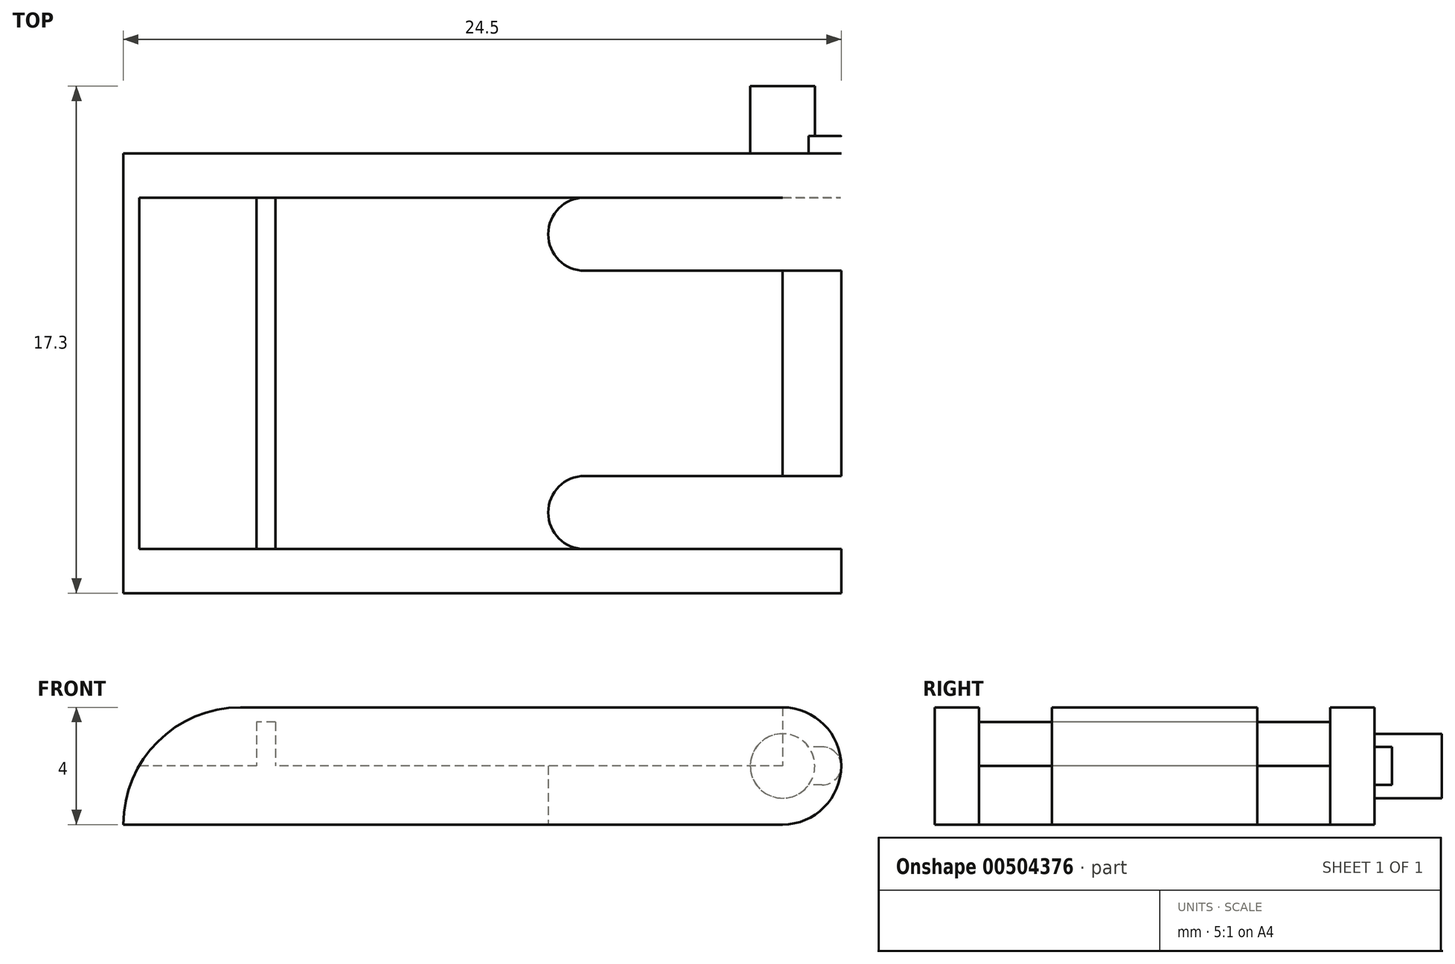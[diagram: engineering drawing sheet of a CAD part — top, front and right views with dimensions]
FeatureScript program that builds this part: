
annotation { "Feature Type Name" : "Feature", "Feature Type Description" : "" }
export const myFeature = defineFeature(function(context is Context, id is Id, definition is map)
    precondition{}
    {
        {
            var Q0;
            Q0=qCreatedBy(makeId("Top.planeOp"),FACE);
            var sketch = newSketch(context, id + "F0", { "sketchPlane" : qUnion([Q0])});
            skLineSegment(sketch, "E0.bottom", {"start": v(0, 0) * mm, "end": v(24.5, 0) * mm});
            skLineSegment(sketch, "E0.top", {"start": v(0, -15) * mm, "end": v(24.5, -15) * mm});
            skLineSegment(sketch, "E0.left", {"start": v(0, 0) * mm, "end": v(0, -15) * mm});
            skLineSegment(sketch, "E0.right", {"start": v(24.5, 0) * mm, "end": v(24.5, -15) * mm});
            skSolve(sketch);
        }
        {
            var Q0;
            Q0=makeQuery(id+"F0.imprint","IMPRINT",FACE,{"disambiguationData":[TD([[makeQuery(id+"F0.imprint","IMPRINT",EDGE,{"derivedFrom":sQuery(id+"F0.wireOp",EDGE,"E0.bottom")}),-1.0]])]});
            extrude(context, id + "F1", {"entities" : qUnion([Q0]), "depth" : 4 * mm});
        }
        {
            var Q0;
            Q0=makeQuery(id+"F1.opExtrude","CAP_FACE",FACE,{"disambiguationData":[OSD([sQuery(id+"F0.wireOp",EDGE,"E0.bottom"),sQuery(id+"F0.wireOp",EDGE,"E0.top"),sQuery(id+"F0.wireOp",EDGE,"E0.left"),sQuery(id+"F0.wireOp",EDGE,"E0.right")])],"isStart":true});
            var sketch = newSketch(context, id + "F2", { "sketchPlane" : qUnion([Q0])});
            skLineSegment(sketch, "E1.bottom", {"start": v(24.5, 11) * mm, "end": v(15.75, 11) * mm});
            skLineSegment(sketch, "E1.top", {"start": v(24.5, 4) * mm, "end": v(15.75, 4) * mm});
            skArc(sketch, "E2", {"start": v(15.75, 13.5) * mm, "mid": v(14.5, 12.25) * mm, "end": v(15.75, 11) * mm});
            skArc(sketch, "E3", {"start": v(15.75, 4) * mm, "mid": v(14.5, 2.75) * mm, "end": v(15.75, 1.5) * mm});
            skLineSegment(sketch, "E4", {"start": v(15.75, 1.5) * mm, "end": v(24.5, 1.5) * mm});
            skLineSegment(sketch, "E5", {"start": v(15.75, 13.5) * mm, "end": v(24.5, 13.5) * mm});
            skLineSegment(sketch, "E6", {"start": v(24.5, 13.5) * mm, "end": v(24.5, 11) * mm});
            skLineSegment(sketch, "E7.trimOffspring", {"start": v(24.5, 4) * mm, "end": v(24.5, 1.5) * mm});
            skLineSegment(sketch, "E8", {"start": v(24.5, 1.5) * mm, "end": v(24.5, 0) * mm, "construction": true});
            skLineSegment(sketch, "E9", {"start": v(24.5, 13.5) * mm, "end": v(24.5, 15) * mm, "construction": true});
            skSolve(sketch);
        }
        {
            var Q0;
            Q0=makeQuery(id+"F2.imprint","IMPRINT",FACE,{"disambiguationData":[TD([[makeQuery(id+"F2.imprint","IMPRINT",EDGE,{"derivedFrom":sQuery(id+"F2.wireOp",EDGE,"E1.bottom")}),-1.0]])]});
            var Q1;
            Q1=makeQuery(id+"F2.imprint","IMPRINT",FACE,{"disambiguationData":[TD([[makeQuery(id+"F2.imprint","IMPRINT",EDGE,{"derivedFrom":sQuery(id+"F2.wireOp",EDGE,"E1.top")}),1.0]])]});
            extrude(context, id + "F3", {"entities" : qUnion([Q0, Q1]), "operationType" : NewBodyOperationType.REMOVE, "oppositeDirection" : true, "depth" : 25 * mm});
        }
        {
            var Q0;
            {var subQ0=sQuery(id+"F0.wireOp",EDGE,"E0.right");var subQ1=sQuery(id+"F0.wireOp",EDGE,"E0.top");Q0=makeQuery(id+"F3.boolean.opBoolean","SPLIT",EDGE,{"disambiguationData":[TD([makeQuery(id+"F1.opExtrude","SWEPT_FACE",FACE,{"disambiguationData":[OSD([subQ1])]})])],"derivedFrom":makeQuery(id+"F1.opExtrude","CAP_EDGE",EDGE,{"disambiguationData":[OSD([subQ0])],"isStart":true})});}
            var Q1;
            {var subQ0=sQuery(id+"F0.wireOp",EDGE,"E0.right");var subQ1=sQuery(id+"F0.wireOp",EDGE,"E0.top");Q1=makeQuery(id+"F3.boolean.opBoolean","SPLIT",EDGE,{"disambiguationData":[TD([makeQuery(id+"F1.opExtrude","SWEPT_FACE",FACE,{"disambiguationData":[OSD([subQ1])]})])],"derivedFrom":makeQuery(id+"F1.opExtrude","CAP_EDGE",EDGE,{"disambiguationData":[OSD([subQ0])],"isStart":false})});}
            var Q2;
            {var subQ0=sQuery(id+"F0.wireOp",EDGE,"E0.right");Q2=makeQuery(id+"F3.boolean.opBoolean","SPLIT",EDGE,{"disambiguationData":[TD([makeQuery(id+"F3.opExtrude","SWEPT_FACE",FACE,{"disambiguationData":[OSD([sQuery(id+"F2.wireOp",EDGE,"E1.bottom")])]})])],"derivedFrom":makeQuery(id+"F1.opExtrude","CAP_EDGE",EDGE,{"disambiguationData":[OSD([subQ0])],"isStart":false})});}
            var Q3;
            {var subQ0=sQuery(id+"F0.wireOp",EDGE,"E0.right");Q3=makeQuery(id+"F3.boolean.opBoolean","SPLIT",EDGE,{"disambiguationData":[TD([makeQuery(id+"F3.opExtrude","SWEPT_FACE",FACE,{"disambiguationData":[OSD([sQuery(id+"F2.wireOp",EDGE,"E1.bottom")])]})])],"derivedFrom":makeQuery(id+"F1.opExtrude","CAP_EDGE",EDGE,{"disambiguationData":[OSD([subQ0])],"isStart":true})});}
            var Q4;
            {var subQ0=sQuery(id+"F0.wireOp",EDGE,"E0.bottom");var subQ1=sQuery(id+"F0.wireOp",EDGE,"E0.right");Q4=makeQuery(id+"F3.boolean.opBoolean","SPLIT",EDGE,{"disambiguationData":[TD([makeQuery(id+"F1.opExtrude","SWEPT_FACE",FACE,{"disambiguationData":[OSD([subQ0])]})])],"derivedFrom":makeQuery(id+"F1.opExtrude","CAP_EDGE",EDGE,{"disambiguationData":[OSD([subQ1])],"isStart":false})});}
            var Q5;
            {var subQ0=sQuery(id+"F0.wireOp",EDGE,"E0.bottom");var subQ1=sQuery(id+"F0.wireOp",EDGE,"E0.right");Q5=makeQuery(id+"F3.boolean.opBoolean","SPLIT",EDGE,{"disambiguationData":[TD([makeQuery(id+"F1.opExtrude","SWEPT_FACE",FACE,{"disambiguationData":[OSD([subQ0])]})])],"derivedFrom":makeQuery(id+"F1.opExtrude","CAP_EDGE",EDGE,{"disambiguationData":[OSD([subQ1])],"isStart":true})});}
            fillet(context, id + "F4", {"entities" : qUnion([Q0, Q1, Q2, Q3, Q4, Q5]), "radius" : 2 * mm, "tangentPropagation" : true, "allowEdgeOverflow" : false});
        }
        {
            var Q0;
            Q0=makeQuery(id+"F1.opExtrude","SWEPT_FACE",FACE,{"disambiguationData":[OSD([sQuery(id+"F0.wireOp",EDGE,"E0.bottom")])]});
            var sketch = newSketch(context, id + "F5", { "sketchPlane" : qUnion([Q0])});
            skCircle(sketch, "E10", {"center": v(-22.5, 2) * mm, "radius": 1.1 * mm});
            skSolve(sketch);
        }
        {
            var Q0;
            Q0=makeQuery(id+"F5.imprint","IMPRINT",FACE,{"disambiguationData":[TD([[makeQuery(id+"F5.imprint","IMPRINT",EDGE,{"derivedFrom":sQuery(id+"F5.wireOp",EDGE,"E10")}),1.0]])]});
            extrude(context, id + "F6", {"entities" : qUnion([Q0]), "operationType" : NewBodyOperationType.ADD, "depth" : 2.3 * mm});
        }
        {
            var Q0;
            Q0=makeQuery(id+"F1.opExtrude","SWEPT_FACE",FACE,{"disambiguationData":[OSD([sQuery(id+"F0.wireOp",EDGE,"E0.bottom")])]});
            var sketch = newSketch(context, id + "F7", { "sketchPlane" : qUnion([Q0])});
            skArc(sketch, "E11", {"start": v(-23.85, 2.65) * mm, "mid": v(-24.5, 2) * mm, "end": v(-23.85, 1.35) * mm});
            skLineSegment(sketch, "E12", {"start": v(-23.85, 2.65) * mm, "end": v(-22.94, 2.65) * mm});
            skLineSegment(sketch, "E13", {"start": v(-22.94, 2.65) * mm, "end": v(-22.94, 1.35) * mm});
            skLineSegment(sketch, "E14", {"start": v(-23.85, 1.35) * mm, "end": v(-22.94, 1.35) * mm});
            skSolve(sketch);
        }
        {
            var Q0;
            {var subQ0=sQuery(id+"F7.wireOp",EDGE,"E12");var subQ1=sQuery(id+"F7.wireOp",EDGE,"E11");var subQ2=makeQuery(id+"F7.imprint","INTERSECT",VERTEX,{"derivedFrom":[subQ1,subQ0]});Q0=makeQuery(id+"F7.imprint","IMPRINT",FACE,{"disambiguationData":[TD([[makeQuery(id+"F7.imprint","IMPRINT",EDGE,{"disambiguationData":[TD([[subQ2,-1.0]])],"derivedFrom":subQ0}),-1.0]])]});}
            extrude(context, id + "F8", {"entities" : qUnion([Q0]), "operationType" : NewBodyOperationType.ADD, "depth" : .6 * mm});
        }
        {
            var Q0;
            Q0=makeQuery(id+"F1.opExtrude","SWEPT_FACE",FACE,{"disambiguationData":[OSD([sQuery(id+"F0.wireOp",EDGE,"E0.bottom")])]});
            cPlane(context, id + "F9", {"entities" : qUnion([Q0]), "cplaneType" : CPlaneType.OFFSET, "offset" : 7.5 * mm, "oppositeDirection" : true, "width" : 150 * mm, "height" : 150 * mm});
        }
        {
            var Q0;
            Q0=makeQuery(id+"F1.opExtrude","CAP_EDGE",EDGE,{"disambiguationData":[OSD([sQuery(id+"F0.wireOp",EDGE,"E0.left")])],"isStart":false});
            fillet(context, id + "F10", {"entities" : qUnion([Q0]), "radius" : 4 * mm, "tangentPropagation" : true, "allowEdgeOverflow" : false});
        }
        {
            var Q0;
            Q0=makeQuery(id+"F1.opExtrude","CAP_FACE",FACE,{"disambiguationData":[OSD([sQuery(id+"F0.wireOp",EDGE,"E0.bottom"),sQuery(id+"F0.wireOp",EDGE,"E0.top"),sQuery(id+"F0.wireOp",EDGE,"E0.left"),sQuery(id+"F0.wireOp",EDGE,"E0.right")])],"isStart":false});
            var sketch = newSketch(context, id + "F11", { "sketchPlane" : qUnion([Q0])});
            skLineSegment(sketch, "E15.bottom", {"start": v(0, -1.5) * mm, "end": v(22.5, -1.5) * mm});
            skLineSegment(sketch, "E15.top", {"start": v(0, -13.5) * mm, "end": v(22.5, -13.5) * mm});
            skLineSegment(sketch, "E15.left", {"start": v(0, -1.5) * mm, "end": v(0, -13.5) * mm});
            skLineSegment(sketch, "E15.right", {"start": v(22.5, -1.5) * mm, "end": v(22.5, -13.5) * mm});
            skSolve(sketch);
        }
        {
            var Q0;
            Q0 = qSketchRegion(id + "F11", true);
            extrude(context, id + "F12", {"entities" : qUnion([Q0]), "operationType" : NewBodyOperationType.REMOVE, "oppositeDirection" : true, "depth" : 2 * mm});
        }
        {
            var Q0;
            Q0=makeQuery(id+"F12.boolean.opBoolean","COPY",FACE,{"derivedFrom":makeQuery(id+"F12.opExtrude","CAP_FACE",FACE,{"disambiguationData":[OSD([sQuery(id+"F11.wireOp",EDGE,"E15.bottom"),sQuery(id+"F11.wireOp",EDGE,"E15.top"),sQuery(id+"F11.wireOp",EDGE,"E15.left"),sQuery(id+"F11.wireOp",EDGE,"E15.right")])],"isStart":false})});
            var sketch = newSketch(context, id + "F13", { "sketchPlane" : qUnion([Q0])});
            skLineSegment(sketch, "E16.bottom", {"start": v(4.54, -1.5) * mm, "end": v(5.19, -1.5) * mm});
            skLineSegment(sketch, "E16.top", {"start": v(4.54, -13.5) * mm, "end": v(5.19, -13.5) * mm});
            skLineSegment(sketch, "E16.left", {"start": v(4.54, -1.5) * mm, "end": v(4.54, -13.5) * mm});
            skLineSegment(sketch, "E16.right", {"start": v(5.19, -1.5) * mm, "end": v(5.19, -13.5) * mm});
            skSolve(sketch);
        }
        {
            var Q0;
            Q0=makeQuery(id+"F13.imprint","IMPRINT",FACE,{"disambiguationData":[TD([[makeQuery(id+"F13.imprint","IMPRINT",EDGE,{"derivedFrom":sQuery(id+"F13.wireOp",EDGE,"E16.bottom")}),1.0]])]});
            extrude(context, id + "F14", {"entities" : qUnion([Q0]), "operationType" : NewBodyOperationType.ADD, "depth" : 1.5 * mm});
        }
    });
